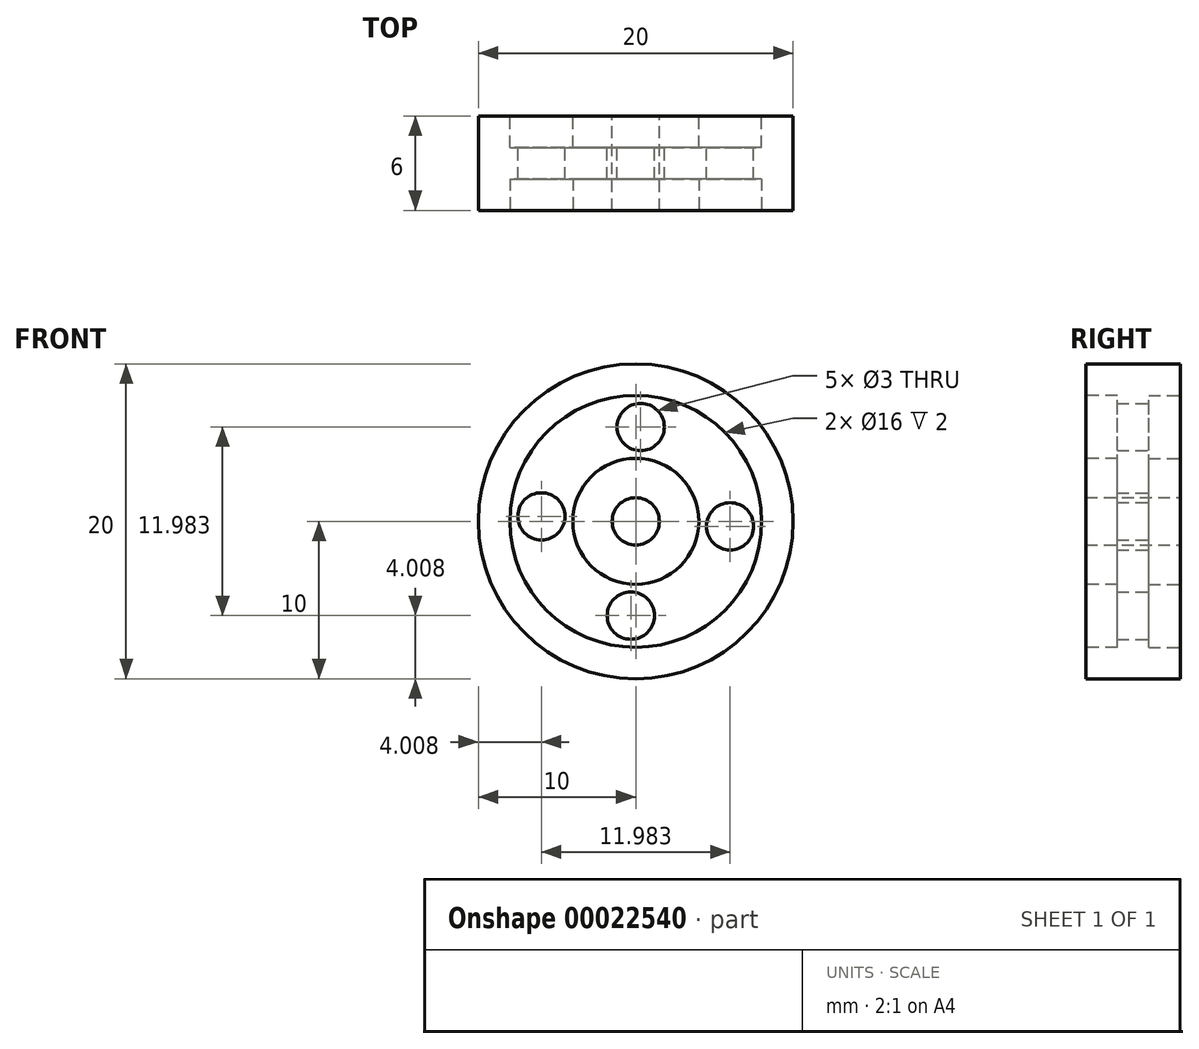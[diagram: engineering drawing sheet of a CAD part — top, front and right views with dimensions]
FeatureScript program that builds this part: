
annotation { "Feature Type Name" : "Feature", "Feature Type Description" : "" }
export const myFeature = defineFeature(function(context is Context, id is Id, definition is map)
    precondition{}
    {
        {
            var Q0;
            Q0=qCreatedBy(makeId("Front.planeOp"),FACE);
            var sketch = newSketch(context, id + "F0", { "sketchPlane" : qUnion([Q0])});
            skCircle(sketch, "E0", {"center": v(0, 0) * mm, "radius": 10 * mm});
            skCircle(sketch, "E1", {"center": v(0, 0) * mm, "radius": 8 * mm});
            skCircle(sketch, "E2", {"center": v(0, 0) * mm, "radius": 4 * mm});
            skCircle(sketch, "E3", {"center": v(0, 0) * mm, "radius": 1.5 * mm});
            skLineSegment(sketch, "E4", {"start": v(0, 0) * mm, "end": v(0.32, 6) * mm});
            skCircle(sketch, "E5", {"center": v(0.32, 6) * mm, "radius": 1.5 * mm});
            skCircle(sketch, "E6.1.0", {"center": v(-6, 0.32) * mm, "radius": 1.5 * mm});
            skCircle(sketch, "E6.2.0", {"center": v(-0.32, -6) * mm, "radius": 1.5 * mm});
            skCircle(sketch, "E6.3.0", {"center": v(6, -0.32) * mm, "radius": 1.5 * mm});
            skSolve(sketch);
        }
        {
            var Q0;
            Q0=makeQuery(id+"F0.imprint","IMPRINT",FACE,{"disambiguationData":[TD([[makeQuery(id+"F0.imprint","IMPRINT",EDGE,{"derivedFrom":sQuery(id+"F0.wireOp",EDGE,"E0")}),1.0]])]});
            var Q1;
            Q1=makeQuery(id+"F0.imprint","IMPRINT",FACE,{"disambiguationData":[TD([[makeQuery(id+"F0.imprint","IMPRINT",EDGE,{"derivedFrom":sQuery(id+"F0.wireOp",EDGE,"E1")}),1.0]])]});
            var Q2;
            Q2=makeQuery(id+"F0.imprint","IMPRINT",FACE,{"disambiguationData":[TD([[makeQuery(id+"F0.imprint","IMPRINT",EDGE,{"derivedFrom":sQuery(id+"F0.wireOp",EDGE,"E3")}),-1.0]])]});
            extrude(context, id + "F1", {"entities" : qUnion([Q0, Q1, Q2]), "depth" : 6 * mm});
        }
        {
            var Q0;
            Q0=makeQuery(id+"F0.imprint","IMPRINT",FACE,{"disambiguationData":[TD([[makeQuery(id+"F0.imprint","IMPRINT",EDGE,{"derivedFrom":sQuery(id+"F0.wireOp",EDGE,"E1")}),1.0]])]});
            extrude(context, id + "F2", {"entities" : qUnion([Q0]), "operationType" : NewBodyOperationType.REMOVE, "depth" : 2 * mm});
        }
        {
            var Q0;
            Q0=makeQuery(id+"F1.opExtrude","CAP_FACE",FACE,{"disambiguationData":[OSD([sQuery(id+"F0.wireOp",EDGE,"E0"),sQuery(id+"F0.wireOp",EDGE,"E3"),sQuery(id+"F0.wireOp",EDGE,"E5"),sQuery(id+"F0.wireOp",EDGE,"E6.1.0"),sQuery(id+"F0.wireOp",EDGE,"E6.2.0"),sQuery(id+"F0.wireOp",EDGE,"E6.3.0")])],"isStart":false});
            var sketch = newSketch(context, id + "F3", { "sketchPlane" : qUnion([Q0])});
            skCircle(sketch, "E7", {"center": v(0, 0) * mm, "radius": 1.5 * mm});
            skCircle(sketch, "E8", {"center": v(0, 0) * mm, "radius": 4 * mm});
            skCircle(sketch, "E9", {"center": v(0, 0) * mm, "radius": 8 * mm});
            skSolve(sketch);
        }
        {
            var Q0;
            Q0=makeQuery(id+"F3.imprint","IMPRINT",FACE,{"disambiguationData":[TD([[makeQuery(id+"F3.imprint","IMPRINT",EDGE,{"derivedFrom":sQuery(id+"F3.wireOp",EDGE,"E8")}),-1.0]])]});
            extrude(context, id + "F4", {"entities" : qUnion([Q0]), "operationType" : NewBodyOperationType.REMOVE, "oppositeDirection" : true, "depth" : 2 * mm});
        }
    });
